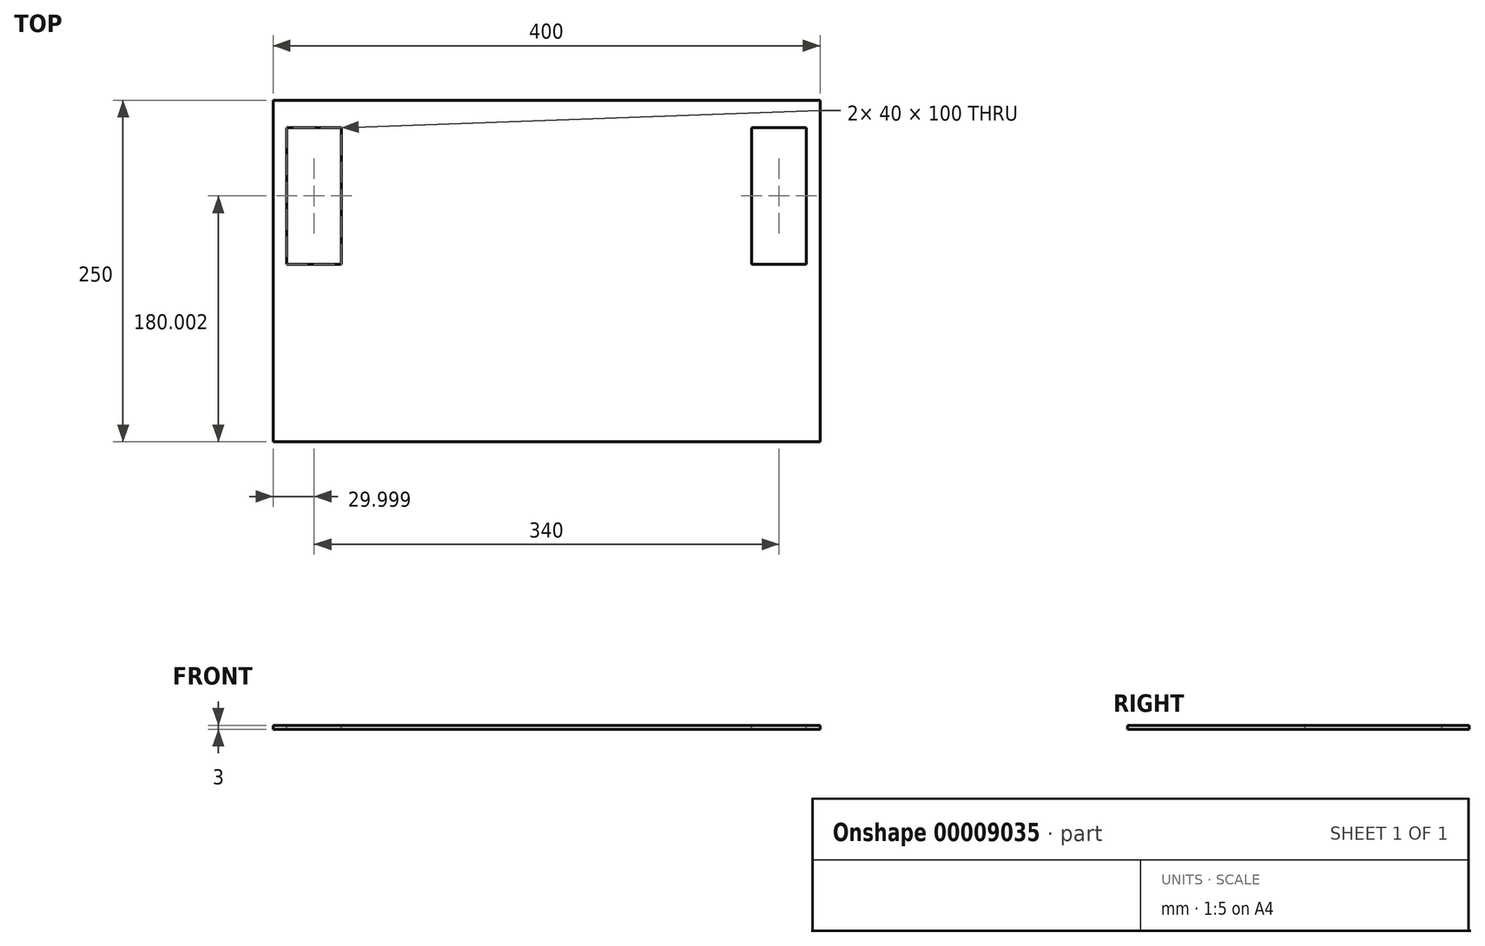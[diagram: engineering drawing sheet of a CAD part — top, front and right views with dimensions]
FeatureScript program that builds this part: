
annotation { "Feature Type Name" : "Feature", "Feature Type Description" : "" }
export const myFeature = defineFeature(function(context is Context, id is Id, definition is map)
    precondition{}
    {
        {
            var Q0;
            Q0=qCreatedBy(makeId("Top.planeOp"),FACE);
            var sketch = newSketch(context, id + "F0", { "sketchPlane" : qUnion([Q0])});
            skLineSegment(sketch, "E0.bottom", {"start": v(-136.2, 111.27) * mm, "end": v(263.8, 111.27) * mm});
            skLineSegment(sketch, "E0.top", {"start": v(-136.2, -138.73) * mm, "end": v(263.8, -138.73) * mm});
            skLineSegment(sketch, "E0.left", {"start": v(-136.2, 111.27) * mm, "end": v(-136.2, -138.73) * mm});
            skLineSegment(sketch, "E0.right", {"start": v(263.8, 111.27) * mm, "end": v(263.8, -138.73) * mm});
            skSolve(sketch);
        }
        {
            var Q0;
            Q0 = qSketchRegion(id + "F0", true);
            extrude(context, id + "F1", {"entities" : qUnion([Q0]), "depth" : 3 * mm});
        }
        {
            var Q0;
            Q0=makeQuery(id+"F1.opExtrude","CAP_FACE",FACE,{"disambiguationData":[OSD([sQuery(id+"F0.wireOp",EDGE,"E0.bottom"),sQuery(id+"F0.wireOp",EDGE,"E0.top"),sQuery(id+"F0.wireOp",EDGE,"E0.left"),sQuery(id+"F0.wireOp",EDGE,"E0.right")])],"isStart":false});
            var sketch = newSketch(context, id + "F2", { "sketchPlane" : qUnion([Q0])});
            skLineSegment(sketch, "E1.bottom", {"start": v(-126.2, 91.27) * mm, "end": v(-86.2, 91.27) * mm});
            skLineSegment(sketch, "E1.top", {"start": v(-126.2, -8.73) * mm, "end": v(-86.2, -8.73) * mm});
            skLineSegment(sketch, "E1.left", {"start": v(-126.2, 91.27) * mm, "end": v(-126.2, -8.73) * mm});
            skLineSegment(sketch, "E1.right", {"start": v(-86.2, 91.27) * mm, "end": v(-86.2, -8.73) * mm});
            skLineSegment(sketch, "E2", {"start": v(63.8, 111.27) * mm, "end": v(63.8, -138.73) * mm, "construction": true});
            skLineSegment(sketch, "E3.0.MirrorCS", {"start": v(253.8, 91.27) * mm, "end": v(213.8, 91.27) * mm});
            skLineSegment(sketch, "E4.0.MirrorCS", {"start": v(253.8, 91.27) * mm, "end": v(253.8, -8.73) * mm});
            skLineSegment(sketch, "E5.0.MirrorCS", {"start": v(253.8, -8.73) * mm, "end": v(213.8, -8.73) * mm});
            skLineSegment(sketch, "E6.0.MirrorCS", {"start": v(213.8, 91.27) * mm, "end": v(213.8, -8.73) * mm});
            skSolve(sketch);
        }
        {
            var Q0;
            Q0 = qSketchRegion(id + "F2", true);
            extrude(context, id + "F3", {"entities" : qUnion([Q0]), "operationType" : NewBodyOperationType.REMOVE, "endBound" : BoundingType.THROUGH_ALL, "oppositeDirection" : true, "depth" : 25 * mm});
        }
    });
